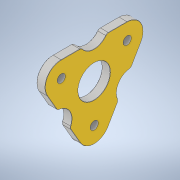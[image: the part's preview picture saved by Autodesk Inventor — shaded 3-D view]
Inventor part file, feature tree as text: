
AUTODESK INVENTOR PART (.ipt)
format: ipt  version: 2021 (Build 250183000, 183)  size: 203,264 bytes
history: native  units: in
note: dims shown in document units (in); Inventor stores cm internally (conversion verified against a paired STEP export)
features: extrude x1, fillet x1, chamfer x1, sketch x1
ambient origin geometry x8: Origin, YZ Plane, XZ Plane, XY Plane, X Axis, Y Axis, Z Axis, Center Point
bodies: Solid1 (feature_tree)
feature tree (4):
  extrude  "Extrusion1"  Depth=0.125in TaperAngle=360.0deg
  fillet  "Fillet2"  Radius=0.125in
  chamfer  "Chamfer3"  Distance=0.125in Angle=45.0deg
  sketch  "Sketch1"  dims[d4=0.325in d5=0.0in d26=1.1811in d28=360.0deg d30=0.125in d31=0.01in d32=0.125in d33=45.0deg]
